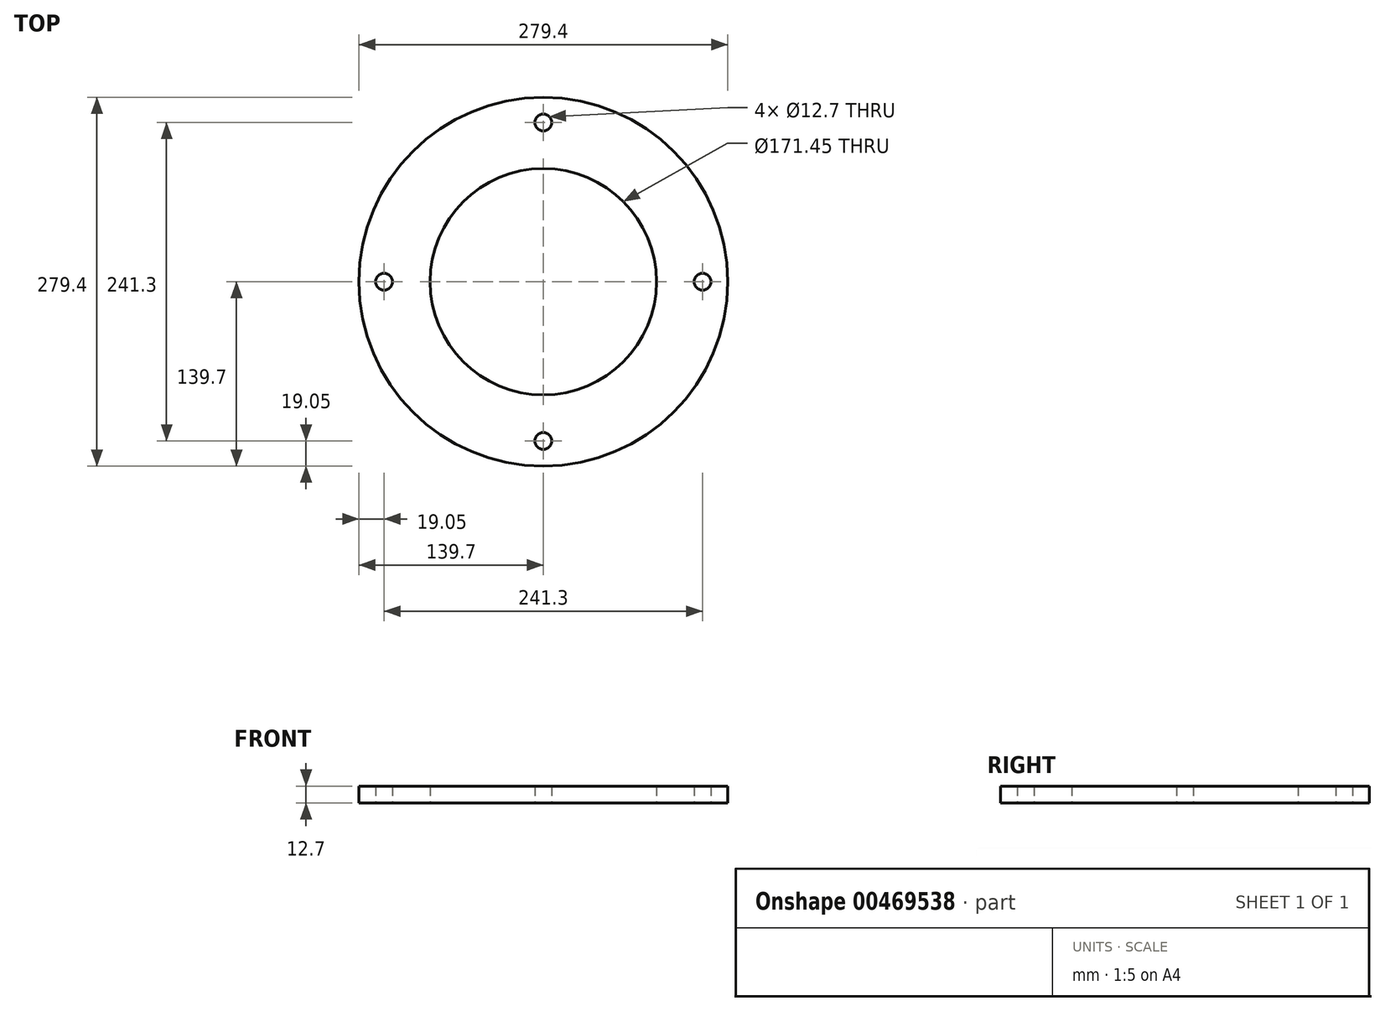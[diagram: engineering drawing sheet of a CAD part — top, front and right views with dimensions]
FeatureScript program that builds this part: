
annotation { "Feature Type Name" : "Feature", "Feature Type Description" : "" }
export const myFeature = defineFeature(function(context is Context, id is Id, definition is map)
    precondition{}
    {
        {
            var Q0;
            Q0=qCreatedBy(makeId("Top.planeOp"),FACE);
            var sketch = newSketch(context, id + "F0", { "sketchPlane" : qUnion([Q0])});
            skCircle(sketch, "E0", {"center": v(0, 0) * mm, "radius": 139.7 * mm});
            skCircle(sketch, "E1", {"center": v(0, 0) * mm, "radius": 85.73 * mm});
            skCircle(sketch, "E2", {"center": v(120.65, 0) * mm, "radius": 6.35 * mm});
            skCircle(sketch, "E3", {"center": v(0, 0) * mm, "radius": 120.65 * mm, "construction": true});
            skCircle(sketch, "E4.1.0", {"center": v(0, 120.65) * mm, "radius": 6.35 * mm});
            skCircle(sketch, "E4.2.0", {"center": v(-120.65, 0) * mm, "radius": 6.35 * mm});
            skCircle(sketch, "E4.3.0", {"center": v(0, -120.65) * mm, "radius": 6.35 * mm});
            skSolve(sketch);
        }
        {
            var Q0;
            Q0 = qSketchRegion(id + "F0", true);
            extrude(context, id + "F1", {"entities" : qUnion([Q0]), "depth" : 12.7 * mm, "offsetDistance" : 25.4 * mm});
        }
    });
